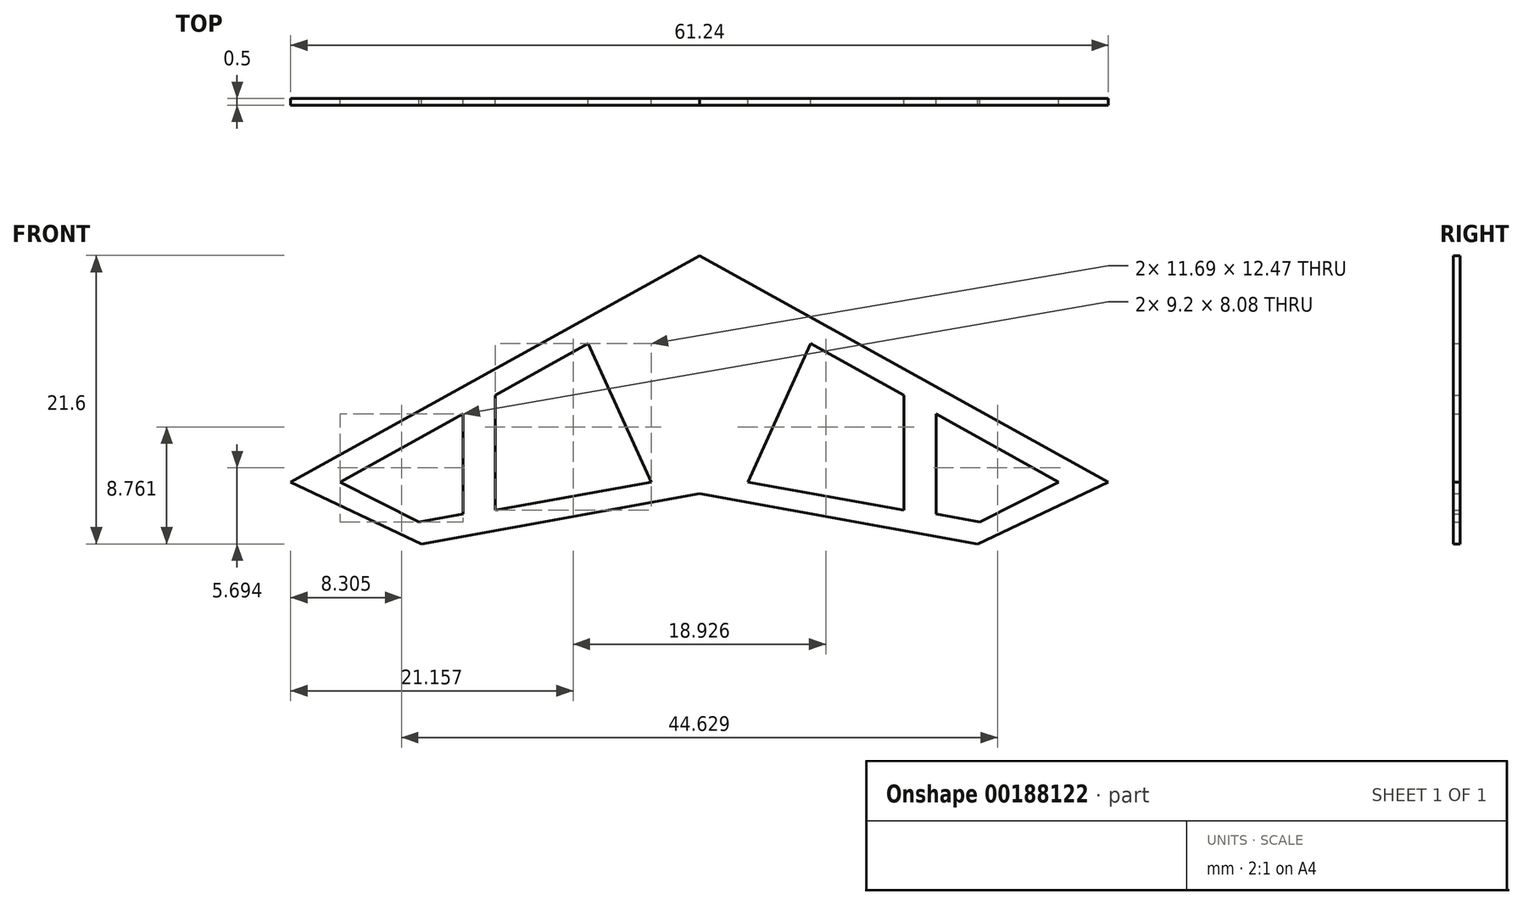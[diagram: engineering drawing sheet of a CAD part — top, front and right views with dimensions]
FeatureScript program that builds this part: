
annotation { "Feature Type Name" : "Feature", "Feature Type Description" : "" }
export const myFeature = defineFeature(function(context is Context, id is Id, definition is map)
    precondition{}
    {
        {
            var Q0;
            Q0=qCreatedBy(makeId("Front.planeOp"),FACE);
            var sketch = newSketch(context, id + "F0", { "sketchPlane" : qUnion([Q0])});
            skLineSegment(sketch, "E0", {"start": v(0, 16.96) * mm, "end": v(-30.62, 0) * mm});
            skLineSegment(sketch, "E1", {"start": v(-30.62, 0) * mm, "end": v(-20.83, -4.64) * mm});
            skLineSegment(sketch, "E2", {"start": v(-20.83, -4.64) * mm, "end": v(0, -0.88) * mm});
            skLineSegment(sketch, "E3", {"start": v(0, -0.88) * mm, "end": v(20.83, -4.64) * mm});
            skLineSegment(sketch, "E4", {"start": v(20.83, -4.64) * mm, "end": v(30.62, 0) * mm});
            skLineSegment(sketch, "E5", {"start": v(30.62, 0) * mm, "end": v(0, 16.96) * mm});
            skLineSegment(sketch, "E6", {"start": v(-3.62, 0) * mm, "end": v(-8.33, 10.36) * mm});
            skLineSegment(sketch, "E7", {"start": v(-8.33, 10.36) * mm, "end": v(-15.3, 6.5) * mm});
            skPoint(sketch, "E7.endSnap0", {"position": v(-15.3, 8.48) * mm});
            skLineSegment(sketch, "E8", {"start": v(-15.3, 6.5) * mm, "end": v(-15.3, -2.11) * mm});
            skLineSegment(sketch, "E9", {"start": v(-15.3, -2.11) * mm, "end": v(-3.62, 0) * mm});
            skLineSegment(sketch, "E10", {"start": v(-21, -2.99) * mm, "end": v(-17.71, -2.4) * mm});
            skLineSegment(sketch, "E11", {"start": v(-17.71, -2.4) * mm, "end": v(-17.71, 5.1) * mm});
            skLineSegment(sketch, "E12", {"start": v(-17.71, 5.1) * mm, "end": v(-26.91, 0) * mm});
            skLineSegment(sketch, "E13", {"start": v(-26.91, 0) * mm, "end": v(-21, -2.99) * mm});
            skLineSegment(sketch, "E14.MirrorCS", {"start": v(3.62, 0) * mm, "end": v(8.33, 10.36) * mm});
            skLineSegment(sketch, "E15.MirrorCS", {"start": v(15.3, -2.11) * mm, "end": v(3.62, 0) * mm});
            skLineSegment(sketch, "E16.MirrorCS", {"start": v(15.3, 6.5) * mm, "end": v(15.3, -2.11) * mm});
            skLineSegment(sketch, "E17.MirrorCS", {"start": v(8.33, 10.36) * mm, "end": v(15.3, 6.5) * mm});
            skLineSegment(sketch, "E18.MirrorCS", {"start": v(17.71, -2.4) * mm, "end": v(17.71, 5.1) * mm});
            skLineSegment(sketch, "E19.MirrorCS", {"start": v(26.91, 0) * mm, "end": v(21, -2.99) * mm});
            skLineSegment(sketch, "E20.MirrorCS", {"start": v(21, -2.99) * mm, "end": v(17.71, -2.4) * mm});
            skLineSegment(sketch, "E21.MirrorCS", {"start": v(17.71, 5.1) * mm, "end": v(26.91, 0) * mm});
            skSolve(sketch);
        }
        {
            var Q0;
            Q0=makeQuery(id+"F0.imprint","IMPRINT",FACE,{"disambiguationData":[TD([[makeQuery(id+"F0.imprint","IMPRINT",EDGE,{"derivedFrom":sQuery(id+"F0.wireOp",EDGE,"E0")}),1.0]])]});
            extrude(context, id + "F1", {"entities" : qUnion([Q0]), "depth" : .5 * mm});
        }
    });
